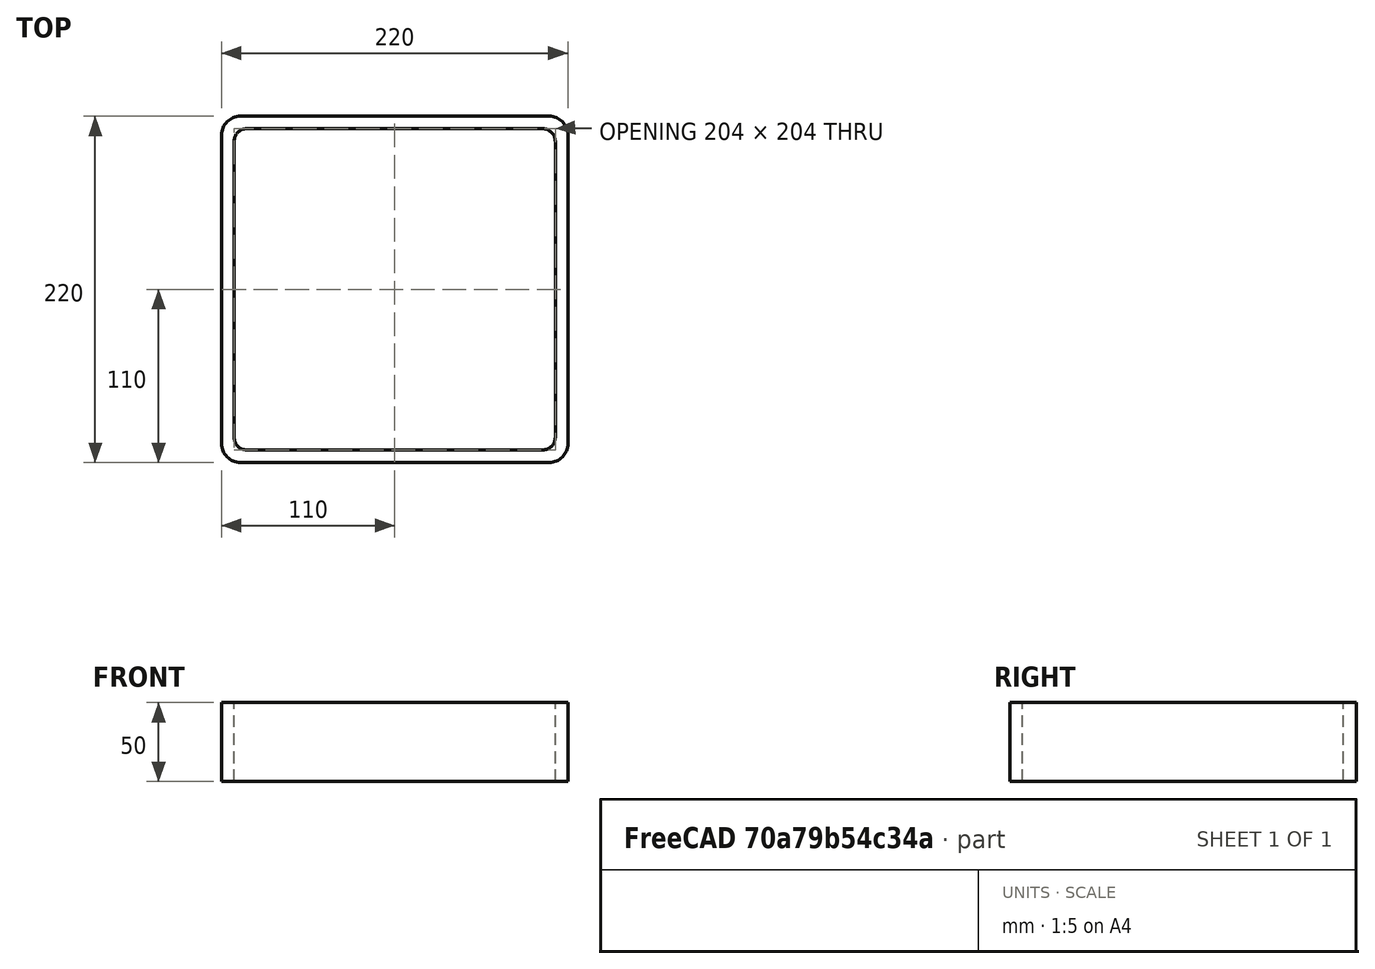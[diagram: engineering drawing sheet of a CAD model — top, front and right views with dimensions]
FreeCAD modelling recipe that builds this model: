
FCSTD DOCUMENT  (FreeCAD 0.15R4671 (Git))
Label: Square hollow section 220x220x8 EN10219 S235JRH
License: All rights reserved
LicenseURL: http://en.wikipedia.org/wiki/All_rights_reserved
objects: Sketcher::SketchObject×1, Part::Extrusion×1
note: 2 computed .brp shape members not serialized (recipe doc carries the construction recipe); baked Part::Feature solids carry a one-line shape summary decoded from their .brp

FEATURE [Sketcher::SketchObject] Sketch
  sketch-geometry (16):
    g0: LineSegment StartX=-94 StartY=102 StartZ=0 EndX=94 EndY=102 EndZ=0
    g1: LineSegment StartX=102 StartY=94 StartZ=0 EndX=102 EndY=-94 EndZ=0
    g2: LineSegment StartX=94 StartY=-102 StartZ=0 EndX=-94 EndY=-102 EndZ=0
    g3: LineSegment StartX=-102 StartY=-94 StartZ=0 EndX=-102 EndY=94 EndZ=0
    g4: LineSegment StartX=-98 StartY=110 StartZ=0 EndX=98 EndY=110 EndZ=0
    g5: LineSegment StartX=110 StartY=98 StartZ=0 EndX=110 EndY=-98 EndZ=0
    g6: LineSegment StartX=98 StartY=-110 StartZ=0 EndX=-98 EndY=-110 EndZ=0
    g7: LineSegment StartX=-110 StartY=-98 StartZ=0 EndX=-110 EndY=98 EndZ=0
    g8: ArcOfCircle CenterX=-94 CenterY=94 CenterZ=0 NormalX=0 NormalY=0 NormalZ=1 Radius=8 StartAngle=1.5708 EndAngle=3.14159
    g9: ArcOfCircle CenterX=94 CenterY=94 CenterZ=0 NormalX=0 NormalY=0 NormalZ=1 Radius=8 StartAngle=0 EndAngle=1.5708
    g10: ArcOfCircle CenterX=94 CenterY=-94 CenterZ=0 NormalX=0 NormalY=0 NormalZ=1 Radius=8 StartAngle=4.71239 EndAngle=6.28319
    g11: ArcOfCircle CenterX=-94 CenterY=-94 CenterZ=0 NormalX=0 NormalY=0 NormalZ=1 Radius=8 StartAngle=3.14159 EndAngle=4.71239
    g12: ArcOfCircle CenterX=98 CenterY=98 CenterZ=0 NormalX=0 NormalY=0 NormalZ=1 Radius=12 StartAngle=0 EndAngle=1.5708
    g13: ArcOfCircle CenterX=98 CenterY=-98 CenterZ=0 NormalX=0 NormalY=0 NormalZ=1 Radius=12 StartAngle=4.71239 EndAngle=6.28319
    g14: ArcOfCircle CenterX=-98 CenterY=-98 CenterZ=0 NormalX=0 NormalY=0 NormalZ=1 Radius=12 StartAngle=3.14159 EndAngle=4.71239
    g15: ArcOfCircle CenterX=-98 CenterY=98 CenterZ=0 NormalX=0 NormalY=0 NormalZ=1 Radius=12 StartAngle=1.5708 EndAngle=3.14159
  constraints (36):
    c: Horizontal(g2)
    c: Vertical(g3)
    c: Horizontal(g6)
    c: Vertical(g7)
    c: Tangent(g3,g8) = 1.5708
    c: Tangent(g0,g8) = 1.5708
    c: Tangent(g0,g9) = 1.5708
    c: Tangent(g1,g9) = 1.5708
    c: Tangent(g1,g10) = 1.5708
    c: Tangent(g2,g10) = 1.5708
    c: Tangent(g2,g11) = 1.5708
    c: Tangent(g3,g11) = 1.5708
    c: Tangent(g4,g12) = 1.5708
    c: Tangent(g5,g12) = 1.5708
    c: Tangent(g5,g13) = 1.5708
    c: Tangent(g6,g13) = 1.5708
    c: Tangent(g6,g14) = 1.5708
    c: Tangent(g7,g14) = 1.5708
    c: Tangent(g7,g15) = 1.5708
    c: Tangent(g4,g15) = 1.5708
    c: Equal(g9,g8)
    c: Equal(g9,g11)
    c: Equal(g9,g10)
    c: Equal(g12,g15)
    c: Equal(g12,g14)
    c: Equal(g12,g13)
    c: Symmetric(g4,g6,g-1)
    c: Symmetric(g7,g5,g-2)
    c: DistanceY(g4,g6) = -220
    c: DistanceX(g7,g5) = 220
    c: Symmetric(g3,g1,g-2)
    c: Symmetric(g0,g2,g-1)
    c: DistanceY(g0,g4) = 8
    c: DistanceX(g5,g1) = -8
    c: Radius(g9) = 8
    c: Radius(g12) = 12
FEATURE [Part::Extrusion] Extrude  label="Square hollow section 220x220x8 EN10219 S235JRH"
  Base = -> Sketch
  Dir = (0,0,50)
  Solid = true
